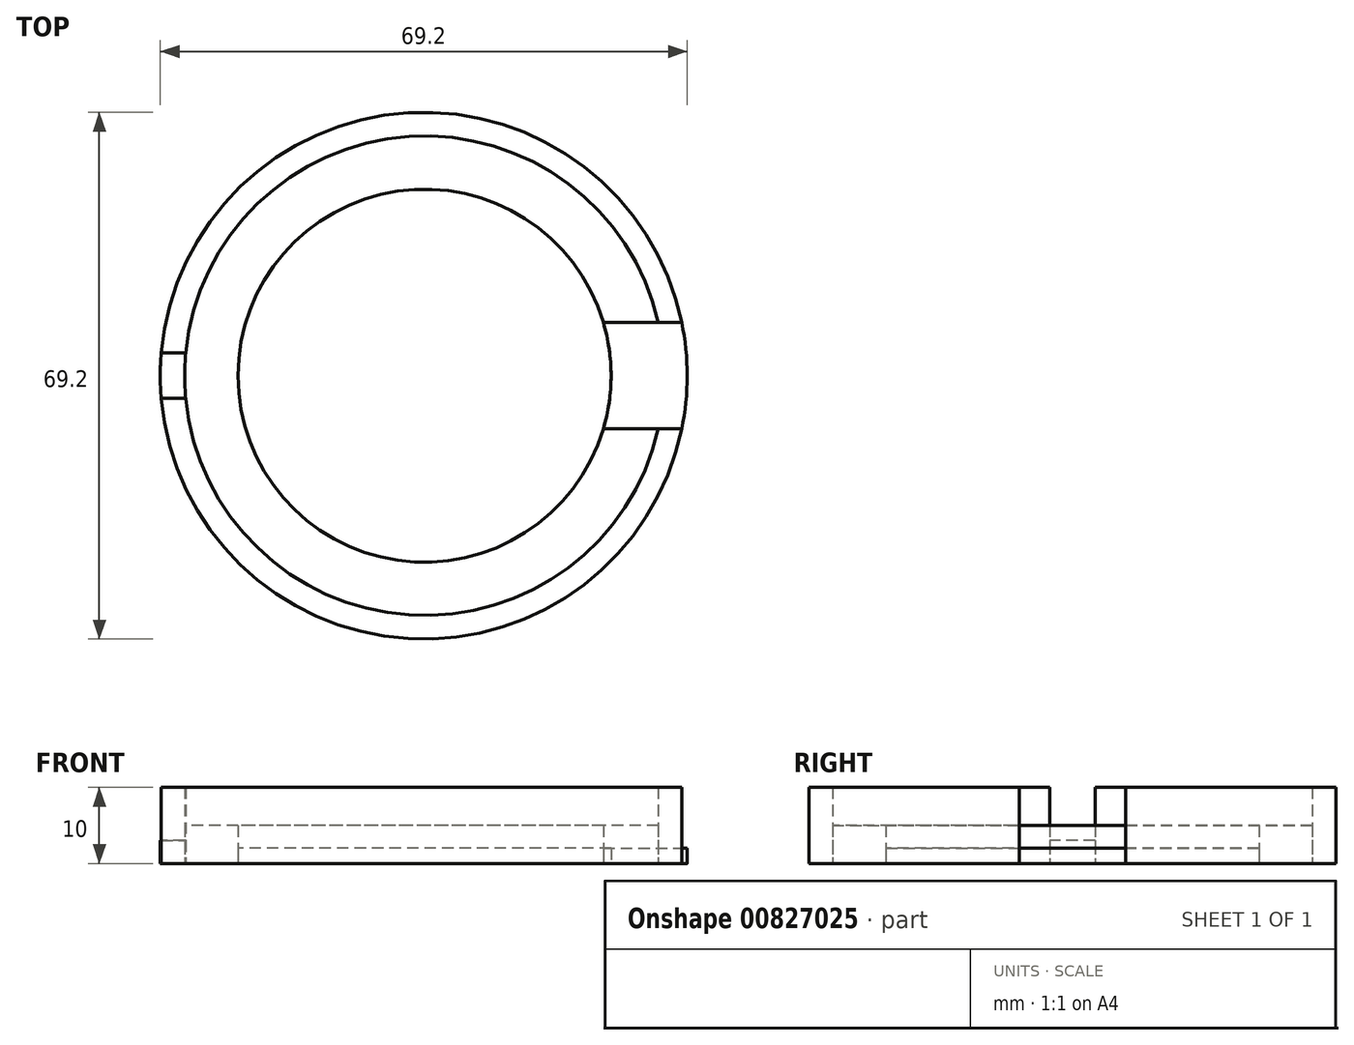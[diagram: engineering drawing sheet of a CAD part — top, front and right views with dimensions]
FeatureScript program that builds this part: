
annotation { "Feature Type Name" : "Feature", "Feature Type Description" : "" }
export const myFeature = defineFeature(function(context is Context, id is Id, definition is map)
    precondition{}
    {
        {
            var Q0;
            Q0=qCreatedBy(makeId("Top.planeOp"),FACE);
            var sketch = newSketch(context, id + "F0", { "sketchPlane" : qUnion([Q0])});
            skLineSegment(sketch, "E0", {"start": v(0.1, 0) * mm, "end": v(24.6, 0) * mm});
            skCircle(sketch, "E1", {"center": v(0.1, 0) * mm, "radius": 24.5 * mm});
            skLineSegment(sketch, "E2", {"start": v(24.6, 0) * mm, "end": v(34.6, 0) * mm});
            skCircle(sketch, "E3", {"center": v(0, 0) * mm, "radius": 34.6 * mm});
            skLineSegment(sketch, "E4", {"start": v(34.6, 0) * mm, "end": v(31.6, 0) * mm});
            skCircle(sketch, "E5", {"center": v(0.1, 0) * mm, "radius": 31.5 * mm});
            skLineSegment(sketch, "E6", {"start": v(-31.4, -3) * mm, "end": v(-31.25, -3) * mm});
            skLineSegment(sketch, "E7", {"start": v(-31.4, 3) * mm, "end": v(-31.25, 3) * mm});
            skLineSegment(sketch, "E8", {"start": v(-31.4, 3) * mm, "end": v(-34.47, 3) * mm});
            skLineSegment(sketch, "E9", {"start": v(-31.4, -3) * mm, "end": v(-34.47, -3) * mm});
            skLineSegment(sketch, "E10", {"start": v(24.6, -7) * mm, "end": v(23.58, -7) * mm});
            skLineSegment(sketch, "E11", {"start": v(23.58, -7) * mm, "end": v(24.6, -7) * mm});
            skLineSegment(sketch, "E12", {"start": v(30.82, -7) * mm, "end": v(24.6, -7) * mm});
            skLineSegment(sketch, "E13", {"start": v(30.82, -7) * mm, "end": v(33.89, -7) * mm});
            skLineSegment(sketch, "E14", {"start": v(24.6, 7) * mm, "end": v(23.58, 7) * mm});
            skLineSegment(sketch, "E15", {"start": v(23.58, 7) * mm, "end": v(24.6, 7) * mm});
            skLineSegment(sketch, "E16", {"start": v(24.6, 7) * mm, "end": v(30.82, 7) * mm});
            skLineSegment(sketch, "E17", {"start": v(30.82, 7) * mm, "end": v(33.89, 7) * mm});
            skSolve(sketch);
        }
        {
            var Q0;
            {var subQ3=sQuery(id+"F0.wireOp",EDGE,"E7");Q0=makeQuery(id+"F0.imprint","IMPRINT",FACE,{"disambiguationData":[TD([[makeQuery(id+"F0.imprint","IMPRINT",EDGE,{"derivedFrom":subQ3}),1.0]])]});}
            var Q1;
            {var subQ0=sQuery(id+"F0.wireOp",EDGE,"E6");Q1=makeQuery(id+"F0.imprint","IMPRINT",FACE,{"disambiguationData":[TD([[makeQuery(id+"F0.imprint","IMPRINT",EDGE,{"derivedFrom":subQ0}),-1.0]])]});}
            extrude(context, id + "F1", {"entities" : qUnion([Q0, Q1]), "depth" : 10 * mm, "offsetDistance" : 25 * mm});
        }
        {
            var Q0;
            {var subQ1=sQuery(id+"F0.wireOp",EDGE,"E6");Q0=makeQuery(id+"F0.imprint","IMPRINT",FACE,{"disambiguationData":[TD([[makeQuery(id+"F0.imprint","IMPRINT",EDGE,{"derivedFrom":subQ1}),1.0]])]});}
            extrude(context, id + "F2", {"entities" : qUnion([Q0]), "depth" : 3 * mm, "offsetDistance" : 25 * mm});
        }
        {
            var Q0;
            {var subQ0=sQuery(id+"F0.wireOp",EDGE,"E1");var subQ1=makeQuery(id+"F0.imprint","INTERSECT",VERTEX,{"derivedFrom":[subQ0,sQuery(id+"F0.wireOp",EDGE,"E2")]});Q0=makeQuery(id+"F0.imprint","IMPRINT",FACE,{"disambiguationData":[TD([[makeQuery(id+"F0.imprint","IMPRINT",EDGE,{"disambiguationData":[TD([[subQ1,-1.0]])],"derivedFrom":subQ0}),1.0]])]});}
            extrude(context, id + "F3", {"entities" : qUnion([Q0]), "depth" : 2 * mm, "offsetDistance" : 25 * mm});
        }
        {
            var Q0;
            {var subQ4=sQuery(id+"F0.wireOp",EDGE,"E10");Q0=makeQuery(id+"F0.imprint","IMPRINT",FACE,{"disambiguationData":[TD([[makeQuery(id+"F0.imprint","IMPRINT",EDGE,{"derivedFrom":subQ4}),1.0]])]});}
            extrude(context, id + "F4", {"entities" : qUnion([Q0]), "depth" : 5 * mm, "offsetDistance" : 25 * mm});
        }
        {
            var Q0;
            {var subQ0=sQuery(id+"F0.wireOp",EDGE,"E14");Q0=makeQuery(id+"F0.imprint","IMPRINT",FACE,{"disambiguationData":[TD([[makeQuery(id+"F0.imprint","IMPRINT",EDGE,{"derivedFrom":subQ0}),1.0]])]});}
            var Q1;
            {var subQ0=sQuery(id+"F0.wireOp",EDGE,"E10");Q1=makeQuery(id+"F0.imprint","IMPRINT",FACE,{"disambiguationData":[TD([[makeQuery(id+"F0.imprint","IMPRINT",EDGE,{"derivedFrom":subQ0}),-1.0]])]});}
            var Q2;
            {var subQ5=sQuery(id+"F0.wireOp",EDGE,"E13");Q2=makeQuery(id+"F0.imprint","IMPRINT",FACE,{"disambiguationData":[TD([[makeQuery(id+"F0.imprint","IMPRINT",EDGE,{"derivedFrom":subQ5}),1.0]])]});}
            var Q3;
            {var subQ5=sQuery(id+"F0.wireOp",EDGE,"E17");Q3=makeQuery(id+"F0.imprint","IMPRINT",FACE,{"disambiguationData":[TD([[makeQuery(id+"F0.imprint","IMPRINT",EDGE,{"derivedFrom":subQ5}),-1.0]])]});}
            extrude(context, id + "F5", {"entities" : qUnion([Q0, Q1, Q2, Q3]), "depth" : 2 * mm, "offsetDistance" : 25 * mm});
        }
    });
